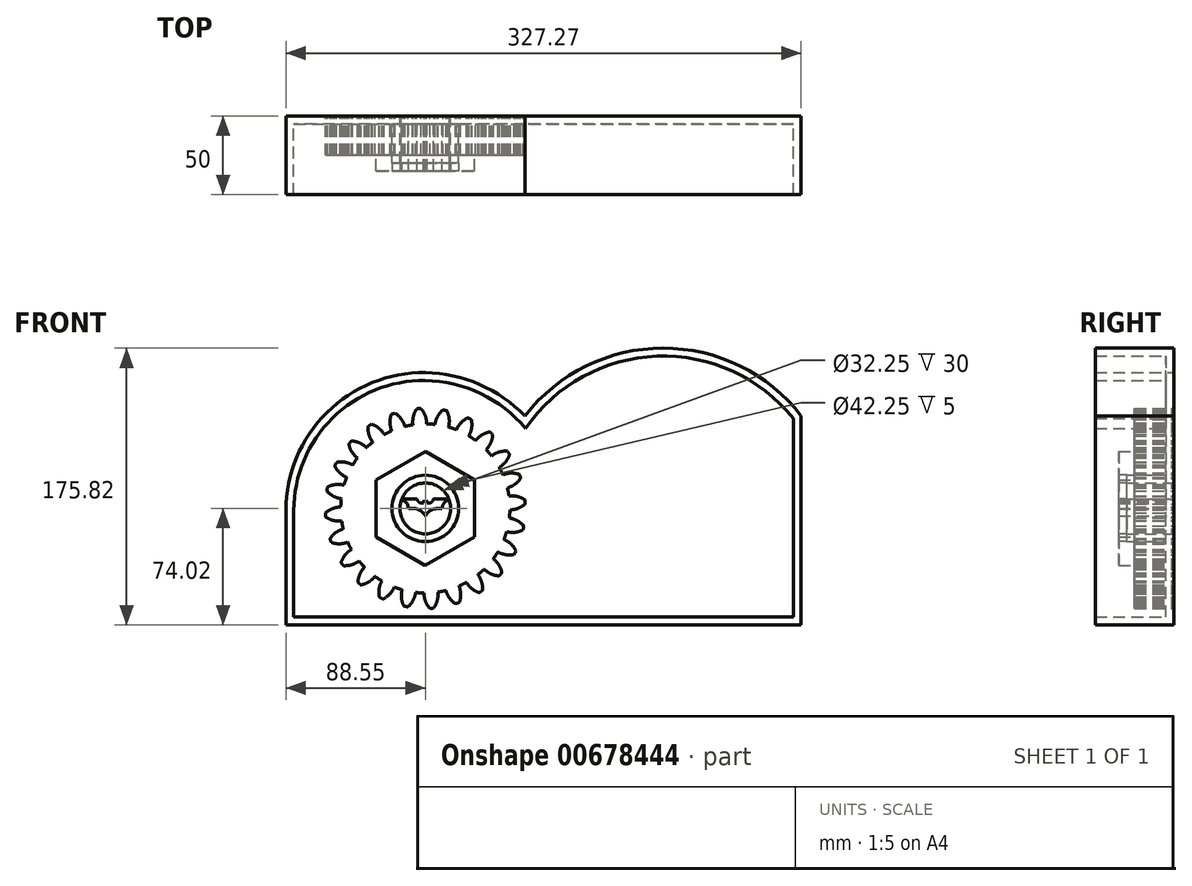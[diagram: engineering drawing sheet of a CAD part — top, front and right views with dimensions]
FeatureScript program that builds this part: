
annotation { "Feature Type Name" : "Feature", "Feature Type Description" : "" }
export const myFeature = defineFeature(function(context is Context, id is Id, definition is map)
    precondition{}
    {
        {
            var Q0;
            Q0=qCreatedBy(makeId("Front.planeOp"),FACE);
            var sketch = newSketch(context, id + "F0", { "sketchPlane" : qUnion([Q0])});
            skCircle(sketch, "E0", {"center": v(0, 0) * mm, "radius": 53.72 * mm});
            skCircle(sketch, "E1", {"center": v(0, 0) * mm, "radius": 58.67 * mm, "construction": true});
            skCircle(sketch, "E2", {"center": v(0, 0) * mm, "radius": 63.5 * mm, "construction": true});
            skLineSegment(sketch, "E3", {"start": v(0, 0) * mm, "end": v(0, 90.99) * mm, "construction": true});
            skLineSegment(sketch, "E4", {"start": v(0, 0) * mm, "end": v(-6.34, 96.72) * mm, "construction": true});
            skLineSegment(sketch, "E5", {"start": v(0, 58.67) * mm, "end": v(-59.75, 58.67) * mm, "construction": true});
            skLineSegment(sketch, "E6", {"start": v(0, 58.67) * mm, "end": v(-56.6, 38.07) * mm, "construction": true});
            skCircle(sketch, "E7", {"center": v(0, 0) * mm, "radius": 55.14 * mm, "construction": true});
            skCircle(sketch, "E8", {"center": v(0, 58.67) * mm, "radius": 14.6 * mm, "construction": true});
            skCircle(sketch, "E9", {"center": v(-13.72, 53.68) * mm, "radius": 14.6 * mm, "construction": true});
            skArc(sketch, "E10", {"start": v(0, 58.67) * mm, "mid": v(-1.2, 61.19) * mm, "end": v(-2.86, 63.44) * mm});
            skArc(sketch, "E11", {"start": v(0.88, 53.71) * mm, "mid": v(0.65, 56.23) * mm, "end": v(0, 58.67) * mm});
            skArc(sketch, "E12.MirrorCS", {"start": v(-7.66, 58.17) * mm, "mid": v(-6.8, 60.82) * mm, "end": v(-5.45, 63.27) * mm});
            skArc(sketch, "E13.MirrorCS", {"start": v(-7.88, 53.14) * mm, "mid": v(-7.98, 55.67) * mm, "end": v(-7.66, 58.17) * mm});
            skArc(sketch, "E14", {"start": v(-2.86, 63.44) * mm, "mid": v(-4.16, 63.41) * mm, "end": v(-5.45, 63.27) * mm});
            skCircle(sketch, "E15.cCircle", {"center": v(0, 0) * mm, "radius": 31.32 * mm, "construction": true});
            skLineSegment(sketch, "E15.0", {"start": v(31.27, -18.18) * mm, "end": v(-0.1, -36.17) * mm});
            skLineSegment(sketch, "E15.1", {"start": v(-0.1, -36.17) * mm, "end": v(-31.37, -18) * mm});
            skLineSegment(sketch, "E15.2", {"start": v(-31.37, -18) * mm, "end": v(-31.27, 18.18) * mm});
            skLineSegment(sketch, "E15.3", {"start": v(-31.27, 18.18) * mm, "end": v(0.1, 36.17) * mm});
            skLineSegment(sketch, "E15.4", {"start": v(0.1, 36.17) * mm, "end": v(31.37, 18) * mm});
            skLineSegment(sketch, "E15.5", {"start": v(31.37, 18) * mm, "end": v(31.27, -18.18) * mm});
            skPoint(sketch, "E15.0.midPoint", {"position": v(15.58, -27.17) * mm});
            skLineSegment(sketch, "E16", {"start": v(-15.38, 5.9) * mm, "end": v(-5.26, 5.9) * mm});
            skLineSegment(sketch, "E17", {"start": v(5.05, 5.9) * mm, "end": v(15.36, 5.9) * mm});
            skLineSegment(sketch, "E18", {"start": v(-0.9, 5.3) * mm, "end": v(-1.23, 3.48) * mm});
            skLineSegment(sketch, "E19", {"start": v(0.82, 5.3) * mm, "end": v(1.22, 3.48) * mm});
            skLineSegment(sketch, "E20", {"start": v(-0.9, 5.3) * mm, "end": v(-0.56, 4.35) * mm});
            skLineSegment(sketch, "E21", {"start": v(-0.56, 4.35) * mm, "end": v(0.45, 4.35) * mm});
            skLineSegment(sketch, "E22", {"start": v(0.45, 4.35) * mm, "end": v(0.82, 5.3) * mm});
            skArc(sketch, "E23", {"start": v(-5.26, 5.9) * mm, "mid": v(-3.8, 3.76) * mm, "end": v(-1.23, 3.48) * mm});
            skArc(sketch, "E24", {"start": v(1.22, 3.48) * mm, "mid": v(3.72, 3.76) * mm, "end": v(5.05, 5.9) * mm});
            skPoint(sketch, "E25", {"position": v(-10.78, -0.27) * mm});
            skPoint(sketch, "E26", {"position": v(10.74, -0.27) * mm});
            skPoint(sketch, "E27", {"position": v(0, -4.63) * mm});
            skArc(sketch, "E28", {"start": v(-10.78, -0.27) * mm, "mid": v(-12.05, 3.58) * mm, "end": v(-15.38, 5.9) * mm});
            skArc(sketch, "E29", {"start": v(15.36, 5.9) * mm, "mid": v(12, 3.6) * mm, "end": v(10.74, -0.27) * mm});
            skArc(sketch, "E30", {"start": v(0, -4.63) * mm, "mid": v(-4.66, -0.63) * mm, "end": v(-10.78, -0.27) * mm});
            skArc(sketch, "E31", {"start": v(10.74, -0.27) * mm, "mid": v(4.64, -0.65) * mm, "end": v(0, -4.63) * mm});
            skSolve(sketch);
        }
        {
            var Q0;
            Q0=makeQuery(id+"F0.imprint","IMPRINT",FACE,{"disambiguationData":[TD([[makeQuery(id+"F0.imprint","IMPRINT",EDGE,{"derivedFrom":sQuery(id+"F0.wireOp",EDGE,"E10")}),1.0]])]});
            var Q1;
            {var subQ0=sQuery(id+"F0.wireOp",EDGE,"E0");var subQ1=makeQuery(id+"F0.imprint","INTERSECT",VERTEX,{"derivedFrom":[subQ0,sQuery(id+"F0.wireOp",EDGE,"E11")]});Q1=makeQuery(id+"F0.imprint","IMPRINT",FACE,{"disambiguationData":[TD([[makeQuery(id+"F0.imprint","IMPRINT",EDGE,{"disambiguationData":[TD([[subQ1,-1.0]])],"derivedFrom":subQ0}),1.0]])]});}
            extrude(context, id + "F1", {"entities" : qUnion([Q0, Q1]), "depth" : 25 * mm, "offsetDistance" : 25 * mm});
        }
        {
            var Q0;
            Q0=makeQuery(id+"F1.opExtrude","SWEPT_BODY",BODY,{"disambiguationData":[OSD([sQuery(id+"F0.wireOp",EDGE,"E0"),sQuery(id+"F0.wireOp",EDGE,"E10"),sQuery(id+"F0.wireOp",EDGE,"E11"),sQuery(id+"F0.wireOp",EDGE,"E12.MirrorCS"),sQuery(id+"F0.wireOp",EDGE,"E13.MirrorCS"),sQuery(id+"F0.wireOp",EDGE,"E14")])]});
            var Q1;
            Q1=makeQuery(id+"F1.opExtrude","SWEPT_FACE",FACE,{"disambiguationData":[OSD([sQuery(id+"F0.wireOp",EDGE,"E0")])]});
            circularPattern(context, id + "F2", {"entities" : qUnion([Q0]), "axis" : qUnion([Q1]), "angle" : 360 * degree, "instanceCount" : 24, "equalSpace" : true});
        }
        {
            var Q0;
            Q0=makeQuery(id+"F0.imprint","IMPRINT",FACE,{"disambiguationData":[TD([[makeQuery(id+"F0.imprint","IMPRINT",EDGE,{"derivedFrom":sQuery(id+"F0.wireOp",EDGE,"E15.0")}),-1.0]])]});
            extrude(context, id + "F3", {"entities" : qUnion([Q0]), "operationType" : NewBodyOperationType.ADD, "depth" : 35 * mm, "offsetDistance" : 25 * mm});
        }
        {
            var Q0;
            Q0=qCreatedBy(makeId("Front.planeOp"),FACE);
            var sketch = newSketch(context, id + "F4", { "sketchPlane" : qUnion([Q0])});
            skLineSegment(sketch, "E32", {"start": v(-88.55, -74.02) * mm, "end": v(238.72, -74.02) * mm});
            skLineSegment(sketch, "E33", {"start": v(238.72, -74.02) * mm, "end": v(238.72, 58.79) * mm});
            skLineSegment(sketch, "E34", {"start": v(-88.55, -74.02) * mm, "end": v(-88.55, -1.39) * mm});
            skArc(sketch, "E35", {"start": v(0, 86.28) * mm, "mid": v(-62.56, 60.92) * mm, "end": v(-88.55, -1.39) * mm});
            skArc(sketch, "E36", {"start": v(63.3, 58.79) * mm, "mid": v(34.38, 78.81) * mm, "end": v(0, 86.28) * mm});
            skArc(sketch, "E37", {"start": v(238.72, 58.79) * mm, "mid": v(151.01, 101.8) * mm, "end": v(63.3, 58.79) * mm});
            skLineSegment(sketch, "E38", {"start": v(238.72, 58.79) * mm, "end": v(238.72, 58.79) * mm});
            skLineSegment(sketch, "E39", {"start": v(-15.35, 2.31) * mm, "end": v(-5.23, 2.31) * mm});
            skLineSegment(sketch, "E40", {"start": v(5.08, 2.31) * mm, "end": v(15.4, 2.31) * mm});
            skLineSegment(sketch, "E41", {"start": v(-0.86, 1.71) * mm, "end": v(-1.2, -0.1) * mm});
            skLineSegment(sketch, "E42", {"start": v(0.85, 1.71) * mm, "end": v(1.25, -0.1) * mm});
            skLineSegment(sketch, "E43", {"start": v(-0.86, 1.71) * mm, "end": v(-0.53, 0.77) * mm});
            skLineSegment(sketch, "E44", {"start": v(-0.53, 0.77) * mm, "end": v(0.48, 0.77) * mm});
            skLineSegment(sketch, "E45", {"start": v(0.48, 0.77) * mm, "end": v(0.85, 1.71) * mm});
            skArc(sketch, "E46", {"start": v(-5.23, 2.31) * mm, "mid": v(-3.77, 0.18) * mm, "end": v(-1.2, -0.1) * mm});
            skArc(sketch, "E47", {"start": v(1.25, -0.1) * mm, "mid": v(3.75, 0.18) * mm, "end": v(5.08, 2.31) * mm});
            skArc(sketch, "E48", {"start": v(-10.75, -3.86) * mm, "mid": v(-12.02, 0) * mm, "end": v(-15.35, 2.31) * mm});
            skArc(sketch, "E49", {"start": v(15.4, 2.31) * mm, "mid": v(12.04, 0.01) * mm, "end": v(10.77, -3.86) * mm});
            skArc(sketch, "E50", {"start": v(0.03, -8.2) * mm, "mid": v(-4.63, -4.22) * mm, "end": v(-10.75, -3.86) * mm});
            skArc(sketch, "E51", {"start": v(10.77, -3.86) * mm, "mid": v(4.67, -4.23) * mm, "end": v(0.03, -8.2) * mm});
            skCircle(sketch, "E52", {"center": v(0, 0) * mm, "radius": 16.13 * mm});
            skSolve(sketch);
        }
        {
            var Q0;
            Q0=makeQuery(id+"F4.imprint","IMPRINT",FACE,{"disambiguationData":[TD([[makeQuery(id+"F4.imprint","IMPRINT",EDGE,{"derivedFrom":sQuery(id+"F4.wireOp",EDGE,"E32")}),1.0]])]});
            extrude(context, id + "F5", {"entities" : qUnion([Q0]), "depth" : 50 * mm, "offsetDistance" : 25 * mm});
        }
        {
            var Q0;
            Q0=makeQuery(id+"F5.opExtrude","CAP_FACE",FACE,{"disambiguationData":[OSD([sQuery(id+"F4.wireOp",EDGE,"E32"),sQuery(id+"F4.wireOp",EDGE,"E33"),sQuery(id+"F4.wireOp",EDGE,"E34"),sQuery(id+"F4.wireOp",EDGE,"E35"),sQuery(id+"F4.wireOp",EDGE,"E36"),sQuery(id+"F4.wireOp",EDGE,"E37"),sQuery(id+"F4.wireOp",EDGE,"E39"),sQuery(id+"F4.wireOp",EDGE,"E40"),sQuery(id+"F4.wireOp",EDGE,"E41"),sQuery(id+"F4.wireOp",EDGE,"E42"),sQuery(id+"F4.wireOp",EDGE,"E43"),sQuery(id+"F4.wireOp",EDGE,"E44"),sQuery(id+"F4.wireOp",EDGE,"E45"),sQuery(id+"F4.wireOp",EDGE,"E46"),sQuery(id+"F4.wireOp",EDGE,"E47"),sQuery(id+"F4.wireOp",EDGE,"E48"),sQuery(id+"F4.wireOp",EDGE,"E49"),sQuery(id+"F4.wireOp",EDGE,"E50"),sQuery(id+"F4.wireOp",EDGE,"E51")])],"isStart":false});
            shell(context, id + "F6", {"entities" : qUnion([Q0]), "thickness" : 5 * mm});
        }
        {
            var Q0;
            {var subQ0=sQuery(id+"F4.wireOp",EDGE,"E52");var subQ1=sQuery(id+"F4.wireOp",EDGE,"E37");var subQ2=sQuery(id+"F4.wireOp",EDGE,"E36");var subQ3=sQuery(id+"F4.wireOp",EDGE,"E35");var subQ4=sQuery(id+"F4.wireOp",EDGE,"E34");var subQ5=sQuery(id+"F4.wireOp",EDGE,"E33");var subQ6=sQuery(id+"F4.wireOp",EDGE,"E32");Q0=makeQuery(id+"F6.opShell","OFFSET_FACE",FACE,{"disambiguationData":[OSD([subQ6,subQ5,subQ4,subQ3,subQ2,subQ1,subQ0]),TDD([makeQuery(id+"F5.opExtrude","CAP_FACE",FACE,{"disambiguationData":[OSD([subQ6,subQ5,subQ4,subQ3,subQ2,subQ1,subQ0])],"isStart":false})])]});}
            extrude(context, id + "F7", {"entities" : qUnion([Q0]), "operationType" : NewBodyOperationType.REMOVE, "oppositeDirection" : true, "depth" : 20 * mm, "offsetDistance" : 25 * mm});
        }
    });
